# Revit family: Lighting Fixture_High Output ARCHITECTURAL CYLINDER_busSTRUT_BRISS-10L-30K-24
name_source: partatom
category: Lighting Fixtures
units: mm (PartAtom-declared; Revit-internal decimal feet)

## family parameters
Always vertical = Yes
Cut with Voids When Loaded = No
Light Source = Yes
Maintain Annotation Orientation = No
OmniClass Number = 23.80.70.00
OmniClass Title = Lighting
Part Type = Normal
Room Calculation Point = No
Round Connector Dimension = Use Diameter
Shared = No
Work Plane-Based = No

## types (3) — shared parameters
Ampacity = 20 A
Apparent Load = 14 VA
Color Filter = 16777215
Default Elevation = 0' - 0"
Dimming Lamp Color Temperature Shift = <None>
Lamp = LED
Lens = Lens BS
Manufacturer = busSTRUT
Photometric Web File = BRISS-10L-30K-24-B.ies
Rated Voltage = 120 V
Tilt Angle = 0.00°
Type Comments = LIGHTING FIXTUTE
URL = https://busstrut.com
Wattage Comments = 14

## per-type parameters (varying)
| type | Body | Model |
| BRISS-10L-30K-24 Black | Black aluminum BS | BRISS-10L-30K-24-B |
| BRISS-10L-30K-24 White | White aluminum BS | BRISS-10L-30K-24-W |
| BRISS-10L-30K-24 Grey | Grey aluminum BS | BRISS-10L-30K-24-G |

## geometry (parser evidence)
native form markers: Sweep x2
no freeform markers — native parametric forms only
